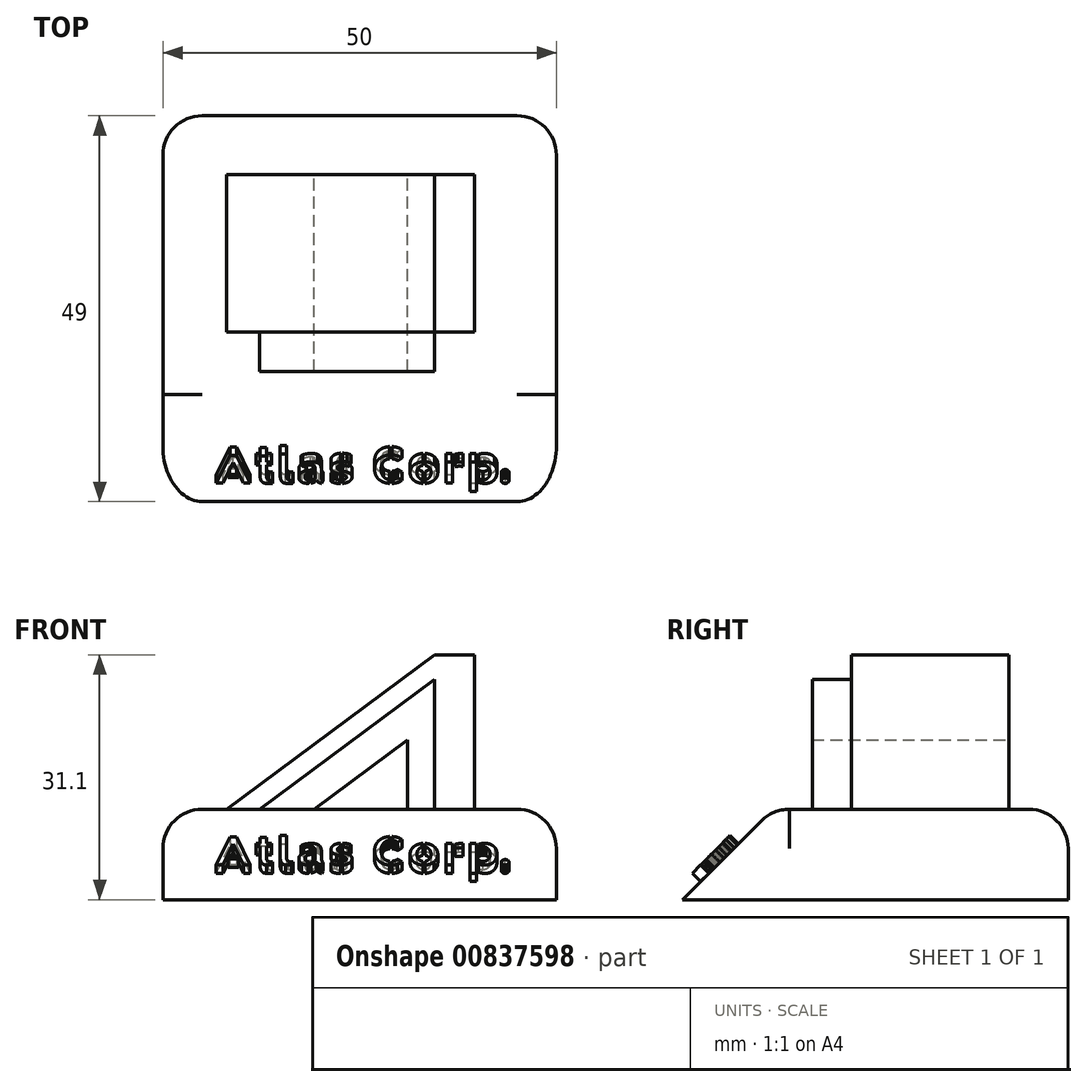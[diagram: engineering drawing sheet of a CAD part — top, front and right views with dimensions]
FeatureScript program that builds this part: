
annotation { "Feature Type Name" : "Feature", "Feature Type Description" : "" }
export const myFeature = defineFeature(function(context is Context, id is Id, definition is map)
    precondition{}
    {
        {
            var Q0;
            Q0=qCreatedBy(makeId("Front.planeOp"),FACE);
            var sketch = newSketch(context, id + "F0", { "sketchPlane" : qUnion([Q0])});
            skLineSegment(sketch, "E0.left", {"start": v(-25, 0) * mm, "end": v(-25, -11.5) * mm});
            skLineSegment(sketch, "E1.MirrorCS", {"start": v(25, 0) * mm, "end": v(25, -11.5) * mm});
            skPoint(sketch, "E0.top.end.orphan", {"position": v(0, -11.5) * mm});
            skLineSegment(sketch, "E2", {"start": v(-25, 0) * mm, "end": v(25, 0) * mm});
            skLineSegment(sketch, "E3", {"start": v(25, -11.5) * mm, "end": v(-25, -11.5) * mm});
            skSolve(sketch);
        }
        {
            var Q0;
            Q0=makeQuery(id+"F0.imprint","IMPRINT",FACE,{"disambiguationData":[TD([[makeQuery(id+"F0.imprint","IMPRINT",EDGE,{"derivedFrom":sQuery(id+"F0.wireOp",EDGE,"E0.left")}),1.0]])]});
            extrude(context, id + "F1", {"entities" : qUnion([Q0]), "depth" : 50 * mm, "offsetDistance" : 25 * mm});
        }
        {
            var Q0;
            Q0=makeQuery(id+"F1.opExtrude","CAP_EDGE",EDGE,{"disambiguationData":[OSD([sQuery(id+"F0.wireOp",EDGE,"E2")])],"isStart":false});
            chamfer(context, id + "F2", {"entities" : qUnion([Q0]), "width" : 20 * mm, "tangentPropagation" : true});
        }
        {
            var Q0;
            Q0=makeQuery(id+"F1.opExtrude","CAP_FACE",FACE,{"disambiguationData":[OSD([sQuery(id+"F0.wireOp",EDGE,"E0.left"),sQuery(id+"F0.wireOp",EDGE,"E1.MirrorCS"),sQuery(id+"F0.wireOp",EDGE,"E2"),sQuery(id+"F0.wireOp",EDGE,"E3")])],"isStart":true});
            extrude(context, id + "F3", {"entities" : qUnion([Q0]), "operationType" : NewBodyOperationType.ADD, "depth" : 7.5 * mm, "offsetDistance" : 25 * mm});
        }
        {
            var Q0;
            Q0=makeQuery(id+"F2.opChamfer","BLEND_FACE",FACE,{"disambiguationData":[OSD([sQuery(id+"F0.wireOp",EDGE,"E2")])]});
            cPlane(context, id + "F4", {"entities" : qUnion([Q0]), "cplaneType" : CPlaneType.OFFSET, "offset" : 0 * mm, "width" : 150 * mm, "height" : 150 * mm});
        }
        {
            var Q0;
            Q0=qCreatedBy(makeId("Front.planeOp"),FACE);
            var sketch = newSketch(context, id + "F5", { "sketchPlane" : qUnion([Q0])});
            skLineSegment(sketch, "E4.bottom", {"start": v(14.6, 0) * mm, "end": v(9.53, 0) * mm});
            skLineSegment(sketch, "E4.top", {"start": v(14.6, 19.6) * mm, "end": v(9.53, 19.6) * mm});
            skLineSegment(sketch, "E4.left", {"start": v(14.6, 0) * mm, "end": v(14.6, 19.6) * mm});
            skLineSegment(sketch, "E4.right", {"start": v(9.53, 0) * mm, "end": v(9.53, 16.5) * mm});
            skLineSegment(sketch, "E5", {"start": v(-16.9, 0) * mm, "end": v(14.6, 0) * mm});
            skLineSegment(sketch, "E6", {"start": v(-12.7, 0) * mm, "end": v(9.53, 0) * mm});
            skLineSegment(sketch, "E7", {"start": v(9.53, 16.5) * mm, "end": v(-12.7, 0) * mm});
            skLineSegment(sketch, "E8", {"start": v(9.53, 19.6) * mm, "end": v(-16.9, 0) * mm});
            skLineSegment(sketch, "E9", {"start": v(6.06, 0) * mm, "end": v(6.06, 8.82) * mm});
            skLineSegment(sketch, "E10", {"start": v(6.06, 8.82) * mm, "end": v(-5.82, 0) * mm});
            skLineSegment(sketch, "E11", {"start": v(-5.82, 0) * mm, "end": v(6.06, 0) * mm});
            skSolve(sketch);
        }
        {
            var Q0;
            {var subQ2=sQuery(id+"F5.wireOp",EDGE,"E4.right");Q0=makeQuery(id+"F5.imprint","IMPRINT",FACE,{"disambiguationData":[TD([[makeQuery(id+"F5.imprint","IMPRINT",EDGE,{"derivedFrom":subQ2}),1.0]])]});}
            extrude(context, id + "F6", {"entities" : qUnion([Q0]), "operationType" : NewBodyOperationType.ADD, "depth" : 25 * mm, "offsetDistance" : 25 * mm});
        }
        {
            var Q0;
            Q0=makeQuery(id+"F5.imprint","IMPRINT",FACE,{"disambiguationData":[TD([[makeQuery(id+"F5.imprint","IMPRINT",EDGE,{"derivedFrom":sQuery(id+"F5.wireOp",EDGE,"E4.top")}),1.0]])]});
            extrude(context, id + "F7", {"entities" : qUnion([Q0]), "operationType" : NewBodyOperationType.ADD, "depth" : 20 * mm, "offsetDistance" : 25 * mm});
        }
        {
            var Q0;
            {var subQ0=sQuery(id+"F0.wireOp",EDGE,"E2");var subQ1=sQuery(id+"F0.wireOp",EDGE,"E1.MirrorCS");Q0=makeQuery(id+"F3.boolean.opBoolean","MERGE",EDGE,{"derivedFrom":[makeQuery(id+"F1.opExtrude","SWEPT_EDGE",EDGE,{"disambiguationData":[OSD([subQ1,subQ0])]}),makeQuery(id+"F3.opExtrude","SWEPT_EDGE",EDGE,{"disambiguationData":[OSD([subQ1,subQ0])]})]});}
            var Q1;
            {var subQ0=sQuery(id+"F0.wireOp",EDGE,"E2");var subQ1=sQuery(id+"F0.wireOp",EDGE,"E0.left");Q1=makeQuery(id+"F3.boolean.opBoolean","MERGE",EDGE,{"derivedFrom":[makeQuery(id+"F1.opExtrude","SWEPT_EDGE",EDGE,{"disambiguationData":[OSD([subQ1,subQ0])]}),makeQuery(id+"F3.opExtrude","SWEPT_EDGE",EDGE,{"disambiguationData":[OSD([subQ1,subQ0])]})]});}
            fillet(context, id + "F8", {"entities" : qUnion([Q0, Q1]), "radius" : 5 * mm, "tangentPropagation" : true, "allowEdgeOverflow" : false});
        }
        {
            var Q0;
            Q0=makeQuery(id+"F3.opExtrude","CAP_EDGE",EDGE,{"disambiguationData":[OSD([sQuery(id+"F0.wireOp",EDGE,"E2")])],"isStart":false});
            fillet(context, id + "F9", {"entities" : qUnion([Q0]), "radius" : 5 * mm, "tangentPropagation" : true, "allowEdgeOverflow" : false});
        }
        {
            var Q0;
            Q0=makeQuery(id+"F2.opChamfer","BLEND_EDGE",EDGE,{"blendedFrom":[makeQuery(id+"F1.opExtrude","CAP_EDGE",EDGE,{"disambiguationData":[OSD([sQuery(id+"F0.wireOp",EDGE,"E2")])],"isStart":false}),makeQuery(id+"F1.opExtrude","SWEPT_FACE",FACE,{"disambiguationData":[OSD([sQuery(id+"F0.wireOp",EDGE,"E0.left")])]})],"blendedInto":[makeQuery(id+"F1.opExtrude","SWEPT_FACE",FACE,{"disambiguationData":[OSD([sQuery(id+"F0.wireOp",EDGE,"E0.left")])]})]});
            var Q1;
            Q1=makeQuery(id+"F2.opChamfer","BLEND_EDGE",EDGE,{"blendedFrom":[makeQuery(id+"F1.opExtrude","CAP_EDGE",EDGE,{"disambiguationData":[OSD([sQuery(id+"F0.wireOp",EDGE,"E2")])],"isStart":false}),makeQuery(id+"F1.opExtrude","SWEPT_FACE",FACE,{"disambiguationData":[OSD([sQuery(id+"F0.wireOp",EDGE,"E1.MirrorCS")])]})],"blendedInto":[makeQuery(id+"F1.opExtrude","SWEPT_FACE",FACE,{"disambiguationData":[OSD([sQuery(id+"F0.wireOp",EDGE,"E1.MirrorCS")])]})]});
            fillet(context, id + "F10", {"entities" : qUnion([Q0, Q1]), "radius" : 5 * mm, "tangentPropagation" : true, "allowEdgeOverflow" : false});
        }
        {
            var Q0;
            Q0=qCreatedBy(id+"F4.planeOp",FACE);
            var sketch = newSketch(context, id + "F11", { "sketchPlane" : qUnion([Q0])});
            skText(sketch, "E12", { "text": "Atlas Corp.", "fontName": "AllertaStencil-Regular.ttf"});
            const initialGuessF11  = {"E12": [-0.01864, -0.0327, 1, 0, 0.005]};
            skSetInitialGuess(sketch, initialGuessF11);
            skSolve(sketch);
        }
        {
            var Q0;
            Q0 = qSketchRegion(id + "F11", true);
            extrude(context, id + "F12", {"entities" : qUnion([Q0]), "operationType" : NewBodyOperationType.ADD, "depth" : 1.5 * mm, "offsetDistance" : 25 * mm});
        }
    });
